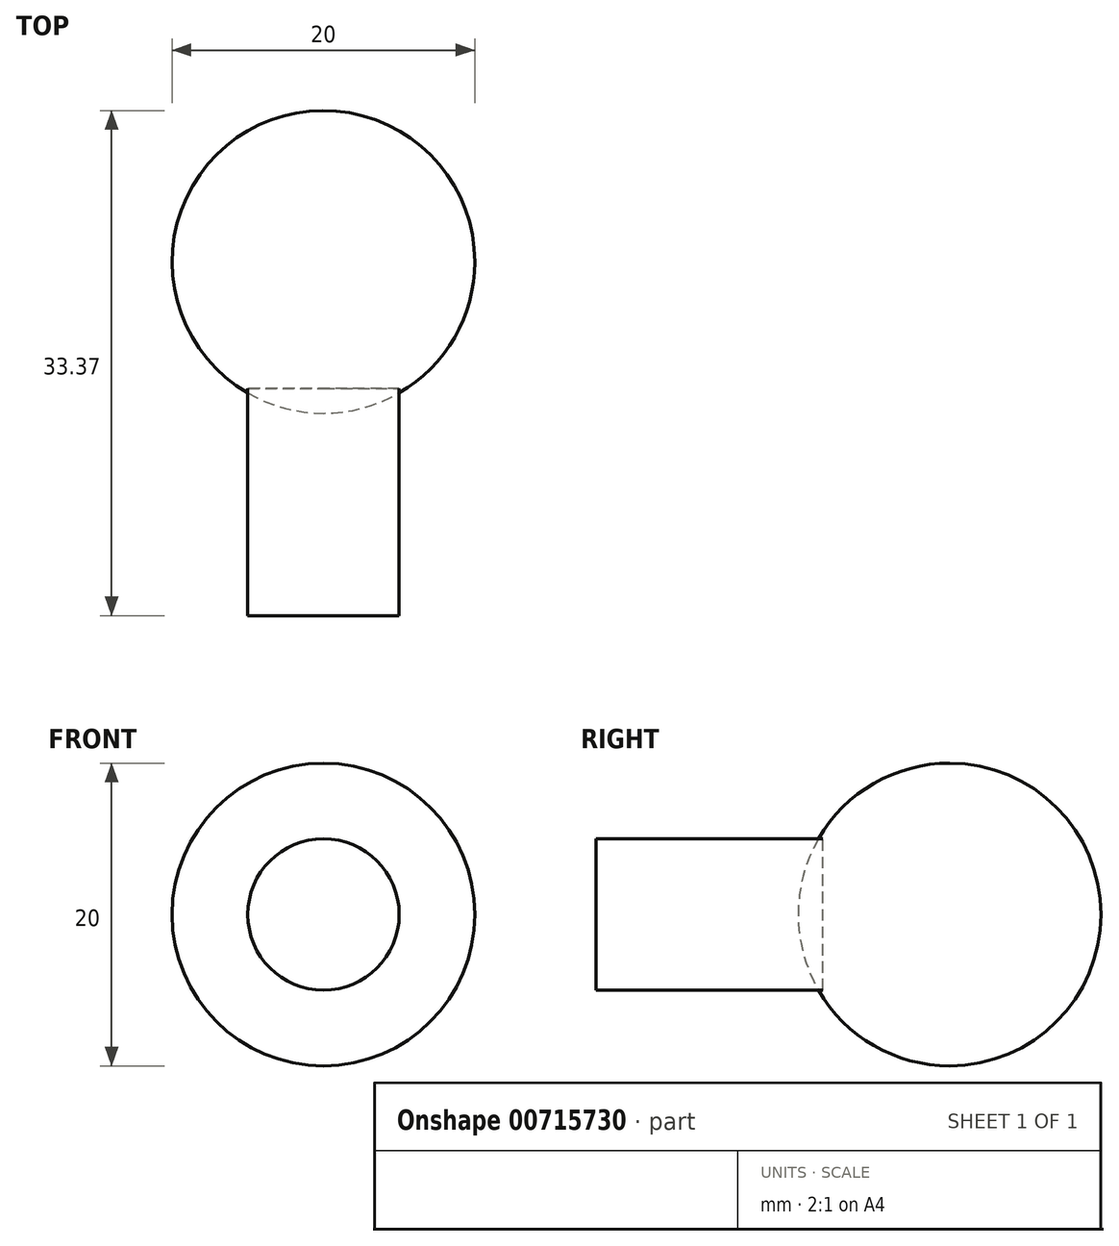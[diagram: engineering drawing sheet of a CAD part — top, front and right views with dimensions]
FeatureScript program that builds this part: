
annotation { "Feature Type Name" : "Feature", "Feature Type Description" : "" }
export const myFeature = defineFeature(function(context is Context, id is Id, definition is map)
    precondition{}
    {
        {
            var Q0;
            Q0=qCreatedBy(makeId("Front.planeOp"),FACE);
            var sketch = newSketch(context, id + "F0", { "sketchPlane" : qUnion([Q0])});
            skCircle(sketch, "E0", {"center": v(0, 0) * mm, "radius": 5 * mm});
            skSolve(sketch);
        }
        {
            var Q0;
            Q0 = qSketchRegion(id + "F0", true);
            extrude(context, id + "F1", {"entities" : qUnion([Q0]), "endBound" : BoundingType.SYMMETRIC, "depth" : 15 * mm, "offsetDistance" : 25 * mm});
        }
        {
            var Q0;
            Q0=qCreatedBy(makeId("Top.planeOp"),FACE);
            var sketch = newSketch(context, id + "F2", { "sketchPlane" : qUnion([Q0])});
            skCircle(sketch, "E1", {"center": v(0, 15.87) * mm, "radius": 10 * mm});
            skSolve(sketch);
        }
        {
            var Q0;
            Q0 = qSketchRegion(id + "F2", true);
            extrude(context, id + "F3", {"entities" : qUnion([Q0]), "endBound" : BoundingType.SYMMETRIC, "depth" : 20 * mm, "offsetDistance" : 25 * mm});
        }
        {
            var Q0;
            Q0=makeQuery(id+"F3.opExtrude","CAP_EDGE",EDGE,{"disambiguationData":[OSD([sQuery(id+"F2.wireOp",EDGE,"E1")])],"isStart":false});
            var Q1;
            Q1=makeQuery(id+"F3.opExtrude","CAP_EDGE",EDGE,{"disambiguationData":[OSD([sQuery(id+"F2.wireOp",EDGE,"E1")])],"isStart":true});
            fillet(context, id + "F4", {"entities" : qUnion([Q0, Q1]), "radius" : 10 * mm, "tangentPropagation" : true, "allowEdgeOverflow" : false});
        }
    });
